# Revit family: PipeFitting_Flange_Table-D_CTS_100-250mm
name_source: partatom
category: Pipe Fittings
units: mm (PartAtom-declared; Revit-internal decimal feet)

## family parameters
Always vertical = Yes
Cut with Voids When Loaded = No
OmniClass Number = 23.60.30.11.14
OmniClass Title = Pipework Fittings
Part Type = Flange
Round Connector Dimension = Use Radius
Shared = No
Work Plane-Based = No

## types (1)
- Standard_Flange_Table-D_CTS_100_250mm
    Assembly Code = D2090800
    Description = T/D Powder Coated CTS Flange
    Lookup Table Name = Flange_Table-D_CTS_100-250mm
    Manufacturer = Reece
    Material = <By Category>
    Model = Standard_Flange_Table-D_CTS_100_250mm
    Model Specification = BMA
    Model Version = 2013-03
    ModifiedIssue_ANZRS = 20130927.63 $
    NATSPECWorkSection = TBC
    OmniclassProducts = TBC
    Type Comments = CTS Copper Capillary Socket Fittings manufactured in accordance with AS 3688.  Adapters meet requirements of a maximum operating pressure of 1.4MPa where working temperature. Electrolysis Insulator made from EDPM rubber to prevent contact from Steel Backing Flange and Copper
    URL = www.reece.com.au
    Uniformat IIElements = TBC

## geometry (parser evidence)
native form markers: Blend x6, Sweep x4
no freeform markers — native parametric forms only
